# Revit family: RVi-IPC41S V.2 (2,8 мм)
name_source: partatom
category: Устройства связи
revit_build: Autodesk Revit 2016 (Build: 20161004_0715(x64)
units: mm (PartAtom-declared; Revit-internal decimal feet)

## family parameters
Всегда вертикально = Да
На основе рабочей плоскости = Да
Общий = Нет
При загрузке вырезать с полостями = Нет
Размер круглого соединителя = Использовать диаметр
Сохранять ориентацию аннотаций = Нет
Тип детали = Нормальный
Точка расчета площади = Нет

## types (4) — shared parameters
2D.Телекамера в герметичном термокожухе = Нет
2D.Телекамера с поворотным устройством = Нет
Bullet.корпус = Корпус 41S_V.2 : Тип
Bullet.крепление = Корпус 41S_V.2.крепление : Тип
Kr_max = 360.00°
Kr_min = -360.00°
RVi.Аудио.Вход = Нет
RVi.Аудио.Выход = Нет
RVi.Аудио.Динамик = Нет
RVi.Аудио.Микрофон = Нет
RVi.ИК подсветка.Дальность = 30000 мм
RVi.Карта памяти = Нет
RVi.Питание 12В = Да
RVi.Питание 24В = Нет
RVi.Питание POE = Да
RVi.Разрешение = 1280×720
RVi.Тип корпуса = Уличные-Bullet
RVi.Тип продукта = Камеры уличные
RVi.Тревога = Нет
RVi.Функция аналитики = Нет
Rn_max = 90.00°
Rn_min = -90.00°
Ro_max = 90.00°
Ro_min = -90.00°
URL = http://rvi-cctv.ru
Ug_max = 83.00°
Ug_min = 82.50°
Uv_max = 53.00°
Uv_min = 52.50°
Группа модели = Камера в сборе
Длина неподвижной части корпуса = 50 мм
Длина подвижной части = 102 мм
Изготовитель = RVi
К идентификации = 250
К обнаружения = 20
К распознавания номера = 240
К распознования = 100
Купол.корпус = Без корпуса : Пусто
Купол.обектив = Без корпуса : Пусто
Купольная камера = Нет
Материал корпуса камеры = Камера.корпус
Материал крепления = Камера.крепление
Материал объектива камеры = Камера.объектив
Наименование и техническая характеристика = "http://rvi-cctv.ru

 "
Обектив коррекция наклона = 90.00°
Отметка по умолчанию = 1219 мм
Поворот направления взгляда = 180.00°
Стрела коррекция = 0.00°
Стрела угол подъема = 0.00°
УГО смещение = 200 мм
да = Да
нет = Нет
zero-valued in all types: Смещение объектива

## per-type parameters (varying)
| type | Вращение всей камеры | Крепление | Стрела длина |
| Крепление MB3 | 0.00° | Крепление MB3 | 55 мм |
| Крепление  380BP + MB3 | 0.00° | Крепление 380BP_MB3 : Сборка | 84 мм |
| Крепление 380BC + MB3 | 45.00° | Крепление 380BC_MB3 : Сборка | 74 мм |
| Стандартная | 0.00° | Без крепления : Пусто | 0 мм |

## geometry (parser evidence)
native form markers: Blend x24
no freeform markers — native parametric forms only
